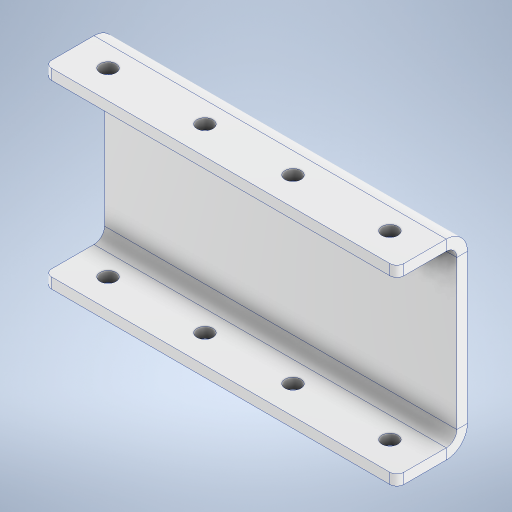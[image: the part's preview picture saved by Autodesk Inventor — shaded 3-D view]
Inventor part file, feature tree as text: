
AUTODESK INVENTOR PART (.ipt)
format: ipt  version: 2024 (Build 280153000, 153)  size: 360,448 bytes
history: native  units: mm
features: other x9, sketch x4, extrude x2, fillet x1
ambient origin geometry x8: Origin, YZ Plane, XZ Plane, XY Plane, X Axis, Y Axis, Z Axis, Center Point
bodies: Volumenkörper1 (feature_tree)
feature tree (16):
  extrude  "Extrusion1"  Depth=3.0mm
  other  "Lasche1"
  other  "Lasche2"
  fillet  "Rundung1"  Radius=3.0mm
  extrude  "Extrusion2"  Depth=3.0mm
  sketch  "Skizze1"  dims[d0=100.0mm d1=42.3mm d2=3.0mm d3=0.0mm]
  sketch  "Skizze2"  dims[d4=3.0mm d5=3.0mm]
  other  "Grobblech1"
  other  "Biegung1"
  other  "Ecke1"
  sketch  "Skizze3"  dims[d6=1.5mm]
  other  "Grobblech2"
  other  "Biegung2"
  other  "Ecke2"
  sketch  "Skizze4"  dims[d7=6.0mm d8=3.0mm d9=20.0mm d10=90.0deg d11=3.0mm d12=12.0mm d13=3.0mm d14=3.0mm d15=3.0mm d16=1.5mm d17=6.0mm d18=3.0mm d19=20.0mm d20=90.0deg d21=3.0mm d22=12.0mm d23=3.0mm d24=3.0mm d25=2.0mm d26=4.5mm d27=4.5mm d28=4.5mm d29=4.5mm d30=25.0mm d31=80.0mm d32=100.0mm d33=0.0mm]
  other  "Definition1"
